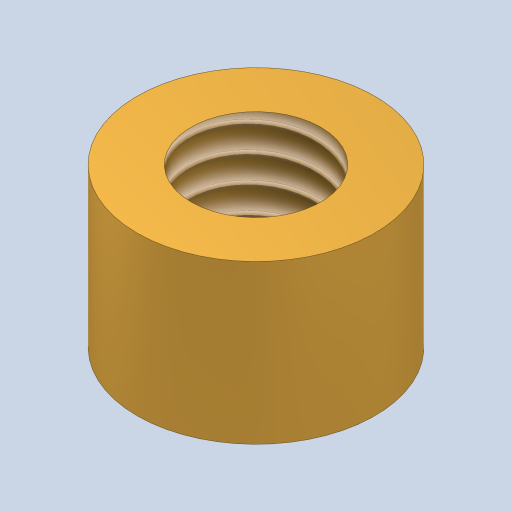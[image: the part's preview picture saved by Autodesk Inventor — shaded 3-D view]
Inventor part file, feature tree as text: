
AUTODESK INVENTOR PART (.ipt)
format: ipt  version: 2023 (Build 270158000, 158)  size: 151,552 bytes
history: native  units: in
note: dims shown in document units (in); Inventor stores cm internally (conversion verified against a paired STEP export)
features: other x1, sketch x1, extrude x1, hole x1
ambient origin geometry x8: Origin, YZ Plane, XZ Plane, XY Plane, X Axis, Y Axis, Z Axis, Center Point
bodies: Body1 (feature_tree)
feature tree (4):
  other  "ソリッド1"
  sketch  "スケッチ1"
  extrude  "押し出し1"  Depth=0.1772in
  hole  "穴1"  [1 undecoded]
note: 1 required parameter value undecoded (feature->parameter linkage not recoverable at this tier; creation-order binding heuristic only, values carry confidence <= 0.55)
